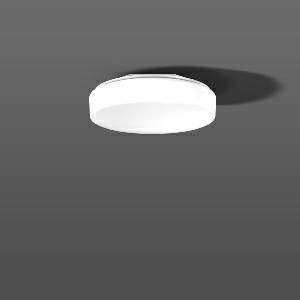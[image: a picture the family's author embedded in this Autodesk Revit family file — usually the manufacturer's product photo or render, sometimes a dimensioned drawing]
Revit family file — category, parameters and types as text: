
# Revit family: flat_polymero_kreis_672478_002_04_a42d
name_source: partatom
category: Lighting Fixtures
units: mm (PartAtom-declared; Revit-internal decimal feet)

## family parameters
Cut with Voids When Loaded = No
Host = Face
Light Source = No
Part Type = Normal
Room Calculation Point = No
Round Connector Dimension = Use Diameter
Shared = No

## types (1)
- FLAT POLYMERO KREIS (1 x LED Modul 830, 1150 lm, 3000)
    Apparent Load = 12 VA
    CIE Flux Codes = 41 72 91 84 100
    Color Rendering = 80
    Color Temperature = 3000
    Default Elevation = 1800 mm
    Description = Series: FLAT POLYMERO KREIS
Decorative round surface-mounted luminaire. For escape route illumination. Base: metal, powder-coated. Diffuser made of non-yellowing plastic (PMMA), opal. Diffuser fastening: patented push system. Suitable for Ceiling mounting, Wall (surface). Self-contained system with automatic self-test and feedback to the RZB monitoring system MULTIDIGIT. 
Colour: white
Diameter: 360 mm
Height: 87 mm
Weight: 1.44 kg
Operating mode: Combined NL readiness
Duration time: 3 h
Lamp: LED
Socket: without socket
Colour temperature: 3000K
Colour rendering index (CRI): 80
System power: 12 W
Rated luminous flux: 1150 lm
Luminous flux, emergency: 170 lm
System power, emergency: -
Control gear: Converter not necessary
Protection class: I
Type of protection: IP 40
    Height = 87 mm
    Lamp = 1 x LED Modul 830
    Lamp Light Flux = 1150 lm
    Lamp count = 1
    Length = 360 mm
    Lifetime = 50000 h
    Luminous efficacy = 96 lm/W
    Manufacturer = RZB
    ModVariant = No
    Model = 672478.002.04
    Mounting Place = Ceiling, Wall
    Mounting Type = Surface mounted
    Number of Poles = 1
    OnlyDefault = Yes
    Power Factor = 1
    Product Name = FLAT POLYMERO KREIS
    Product group = Surface mounted ceiling and wall luminaires
    ProductGroupID = 305
    Protection Class = Protection class I
    Protection Degree = IP 40
    RLX_Detail_Level = 1
    RLX_Emergency_Light_Flux = 170 lm
    RLX_Emergency_Type = 3
    RLX_Emergency_Type_DB = Yes
    RlxData = <blob elided: 52293 chars, md5=228d0331>
    Socket = socket
    Standby Power = 0 W
    System Light Flux = 1150 lm
    System Power = 12 W
    Type Comments = Product without accessories
    Type Image = 672092.002.1.jpg
    URL = http://relux.com
    VarID = ---
    Voltage = 230 V
    Voltage Range = 220-240 V
    Weight = 0.00 kg
    Width = 0 mm  [stored 0 ft]

note: [stored X ft] marks values corroborated as IEEE doubles in the binary element streams (Revit-internal decimal feet)

## geometry (parser evidence)
native form markers: Blend x4, Sweep x15
no freeform markers — native parametric forms only
